# Revit family: 01 DH2 ISLA 985
name_source: partatom
category: Air Terminals
revit_build: Autodesk Revit 2017 (Build: 20160225_1515(x64)
units: mm (PartAtom-declared; Revit-internal decimal feet)

## family parameters
Always vertical = Yes
Cut with Voids When Loaded = No
Host = Wall
OmniClass Number = 23.75.00.00
OmniClass Title = Climate Control (HVAC)
Part Type = Normal
Room Calculation Point = No
Round Connector Dimension = Use Diameter
Shared = No

## types (2) — shared parameters
Acabado_Bandejas = Teka_Bandejas
Acabado_Campana = Teka_Acero Inoxidable Satinado
Alto = 1000 mm  [stored 3.28084 ft]
Ca_1_Frecuencia 50/60 Hz = Yes
Ca_1_Opción de recirculación = Yes
Ca_1_Potencia Iluminación, W. (Led) = 4 x 3W
Ca_1_Potencia motor, W. = 280
Ca_1_Potencia máxima, W. = 292
Ca_1_Reducción opcional Ø 150/ Ø120 mm. = Yes
Ca_1_Salida exterior, mm. = 150
Ca_1_Tensión 220/240 V. = Si
Ca_2_Electrónico = Yes
Ca_2_Pulsante (Retroiluminación) = Yes
Ca_2_Touch Control = No
Ca_3_Filtro metálico decorativo = No
Ca_3_Indicador de saturación de filtros = Yes
Ca_3_Motor Blindado = Yes
Ca_3_N° de Velocidades = 3+1
Ca_3_N° de motores = 1 DT
Ca_3_Panel de fácil limpieza = Yes
Ca_3_Piloto de funcionamiento = Yes
Ca_3_Programación de tiempo de aspiración = Yes
Ca_3_Sensor de humedad = No
Ca_4_Ala de Cristal = No
Ca_4_Ala de acero Inoxidable = Yes
Ca_4_Fabricada en Acero Austenítico Certificado = Yes
Ca_Alto = 600 mm
Ca_Clase de Eficiencia Energética = A
Ca_Creado por = Catálogo Arquitectura
Ca_Código Catálogo Arquitectura = 465_TEK_036
Ca_Código EAN = 8421152145715
Ca_Código del Producto = 40484640
Ca_Fabricante = Teka
Ca_Instalación = Colgante o mural
Ca_Itemizado CDT = E 08 06 02
Ca_Masterformat = 11 30 13.13
Ca_Material Principal = Acero Austenítico Certificado
Ca_Medidas de embalaje = 107 x 70 x 100
Ca_País de Fabricación = España
Ca_Peso = 42,51 kg
Ca_Profundidad = 600 mm
Ca_Representante = Teka
Ca_Teléfono = 99821 1017
Ca_Usos = Campana de extracción y recirculación de cocina
Ca_Web del Fabricante = www.teka.com
Ca_Web del Representante = www.teka.cl
Control_Alto = 1000 mm  [stored 3.28084 ft]
Description = Campana de extracción y recirculación de cocina (NO incluye filtros de Carbón)
Manufacturer = Teka
Model = DH2 Isla 985
URL = www.teka.cl

## per-type parameters (varying)
| type | Ancho | Ca_Ancho | Ca_Especificaciones Técnicas | Ca_Producto |
| DH2 ISLA 985 - 900mm | 900 mm  [stored 2.95276 ft] | 900 mm  [stored 2.95276 ft] | Campana decorativa isla para cocina modelo DH2 Isla 985 de ancho 900mm | Campana decorativa isla DH2 Isla 985 900mm |
| DH2 ISLA 985 - 1200mm | 1200 mm | 1200 mm | Campana decorativa isla para cocina modelo DH2 Isla 985 de ancho 1200mm | Campana decorativa isla DH2 Isla 985 1200mm |

note: [stored X ft] marks values corroborated as IEEE doubles in the binary element streams (Revit-internal decimal feet)

## geometry (parser evidence)
native form markers: Sweep x3
no freeform markers — native parametric forms only
